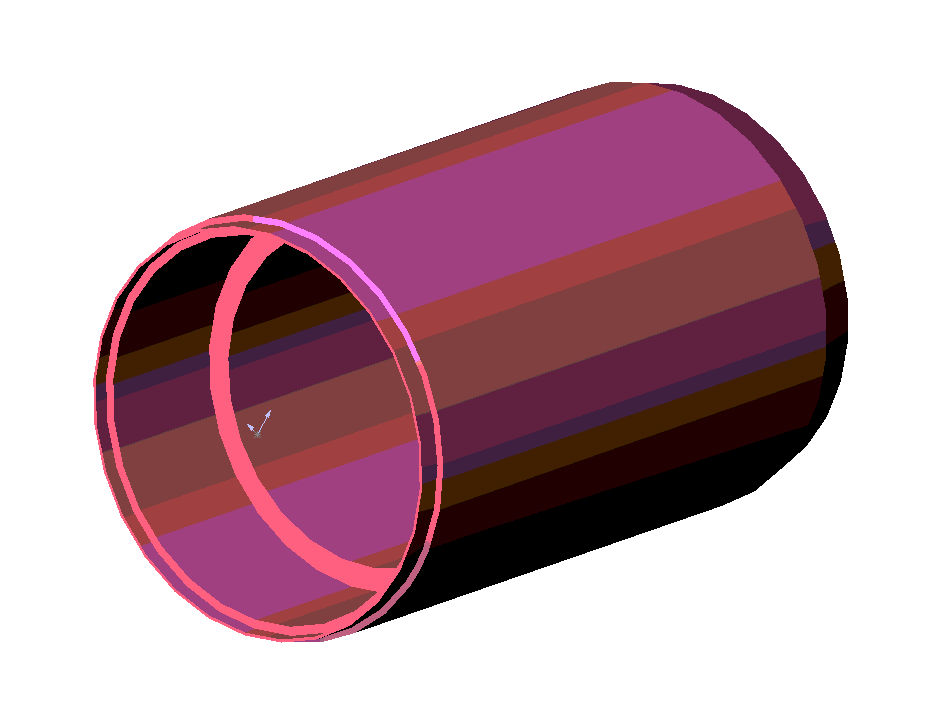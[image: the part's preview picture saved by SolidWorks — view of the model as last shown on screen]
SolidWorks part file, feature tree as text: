
SOLIDWORKS PART (.sldprt)
format: sldprt  version: not decoded by parser v0  size: 126,976 bytes
history: native  units: mm
features: sketch x6, cut_extrude x5, plane x3, chamfer x2, material x1, extrude x1 (+10 scaffold rows collapsed)
feature tree (28):
  scaffold x10  (default folders/planes/origin — collapsed)
  material  "Matériau <non spécifié>"
  plane  "Plan1"
  plane  "Plan2"
  plane  "Plan3"
  sketch  "Esquisse1"  dims[D1=35.0mm D2=28.0mm]
  extrude  "Base-Extrusion"  Depth=54mm
  sketch  "Esquisse2"  dims[D1=30.5mm]
  cut_extrude  "Enlèv. mat.-Extru.1"  Depth=1.5mm
  chamfer  "Chanfrein4"  Distance=4mm Angle=15deg
  sketch  "Esquisse3"  dims[D1=29.0mm]
  cut_extrude  "Enlèv. mat.-Extru.2"  Depth=5mm
  sketch  "Esquisse4"  dims[D1=34.0mm]
  cut_extrude  "Enlèv. mat.-Extru.3"  Depth=2mm
  sketch  "Esquisse5"  dims[D1=32.0mm]
  cut_extrude  "Enlèv. mat.-Extru.4"  Depth=13.3mm
  sketch  "Esquisse6"  dims[D1=33.5mm]
  cut_extrude  "Enlèv. mat.-Extru.5"  Depth=1.3mm
  chamfer  "Chanfrein5"  Distance=0.5mm Angle=15deg
decode coverage: 14 of 14 modeling features carry decoded parameters
note: suppression state not decoded; provenance and decode notes live in map.json
